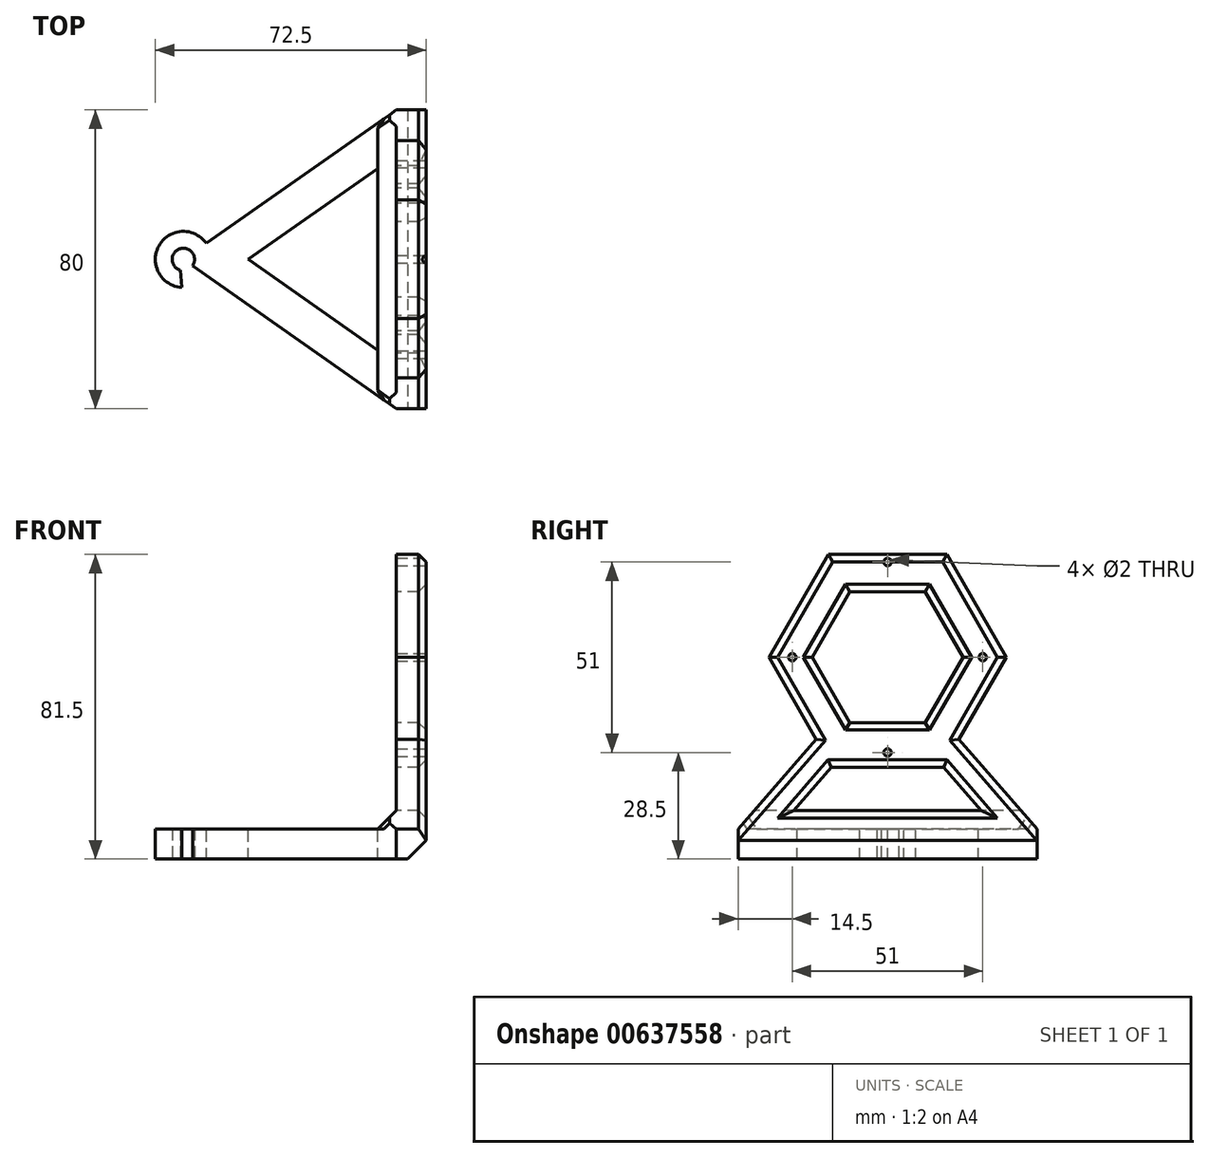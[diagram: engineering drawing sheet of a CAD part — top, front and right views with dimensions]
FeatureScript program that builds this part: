
annotation { "Feature Type Name" : "Feature", "Feature Type Description" : "" }
export const myFeature = defineFeature(function(context is Context, id is Id, definition is map)
    precondition{}
    {
        {
            var Q0;
            Q0=qCreatedBy(makeId("Front.planeOp"),FACE);
            var sketch = newSketch(context, id + "F0", { "sketchPlane" : qUnion([Q0])});
            skLineSegment(sketch, "E0", {"start": v(0, 0) * mm, "end": v(-90, 0) * mm});
            skLineSegment(sketch, "E1", {"start": v(0, 0) * mm, "end": v(0, 100) * mm});
            skLineSegment(sketch, "E2", {"start": v(0, 100) * mm, "end": v(-8, 100) * mm});
            skLineSegment(sketch, "E3", {"start": v(-8, 100) * mm, "end": v(-8, 8) * mm});
            skLineSegment(sketch, "E4", {"start": v(-8, 8) * mm, "end": v(-90, 8) * mm});
            skLineSegment(sketch, "E5", {"start": v(-90, 8) * mm, "end": v(-90, 0) * mm});
            skSolve(sketch);
        }
        {
            var Q0;
            Q0 = qSketchRegion(id + "F0", true);
            extrude(context, id + "F1", {"entities" : qUnion([Q0]), "endBound" : BoundingType.SYMMETRIC, "depth" : 80 * mm, "offsetDistance" : 25 * mm});
        }
        {
            var Q0;
            Q0=makeQuery(id+"F1.opExtrude","SWEPT_FACE",FACE,{"disambiguationData":[OSD([sQuery(id+"F0.wireOp",EDGE,"E0")])]});
            var sketch = newSketch(context, id + "F2", { "sketchPlane" : qUnion([Q0])});
            skCircle(sketch, "E6", {"center": v(-65, 0) * mm, "radius": 3 * mm});
            skSolve(sketch);
        }
        {
            var Q0;
            Q0 = qSketchRegion(id + "F2", true);
            extrude(context, id + "F3", {"entities" : qUnion([Q0]), "operationType" : NewBodyOperationType.REMOVE, "endBound" : BoundingType.THROUGH_ALL, "oppositeDirection" : true, "depth" : 25 * mm, "offsetDistance" : 25 * mm});
        }
        {
            var Q0;
            Q0=makeQuery(id+"F1.opExtrude","SWEPT_FACE",FACE,{"disambiguationData":[OSD([sQuery(id+"F0.wireOp",EDGE,"E1")])]});
            var sketch = newSketch(context, id + "F4", { "sketchPlane" : qUnion([Q0])});
            skLineSegment(sketch, "E7", {"start": v(-40, 100) * mm, "end": v(40, 8) * mm, "construction": true});
            skLineSegment(sketch, "E8", {"start": v(40, 100) * mm, "end": v(-40, 8) * mm, "construction": true});
            skPoint(sketch, "E9", {"position": v(-25.5, 54) * mm});
            skLineSegment(sketch, "E10", {"start": v(0, 54) * mm, "end": v(0, 99.75) * mm, "construction": true});
            skLineSegment(sketch, "E11", {"start": v(0, 54) * mm, "end": v(-45.17, 54) * mm, "construction": true});
            skPoint(sketch, "E12.1.0", {"position": v(0, 28.5) * mm});
            skPoint(sketch, "E12.2.0", {"position": v(25.5, 54) * mm});
            skPoint(sketch, "E12.3.0", {"position": v(0, 79.5) * mm});
            skPoint(sketch, "E12.center", {"position": v(0, 54) * mm});
            skSolve(sketch);
        }
        {
            var Q0;
            Q0=sQuery(id+"F4.wireOp",VERTEX,"E9");
            var Q1;
            Q1=sQuery(id+"F4.wireOp",VERTEX,"E12.3.0");
            var Q2;
            Q2=sQuery(id+"F4.wireOp",VERTEX,"E12.2.0");
            var Q3;
            Q3=sQuery(id+"F4.wireOp",VERTEX,"E12.1.0");
            var Q4;
            Q4=makeQuery(id+"F1.opExtrude","SWEPT_BODY",BODY,{"disambiguationData":[OSD([sQuery(id+"F0.wireOp",EDGE,"E0"),sQuery(id+"F0.wireOp",EDGE,"E1"),sQuery(id+"F0.wireOp",EDGE,"E2"),sQuery(id+"F0.wireOp",EDGE,"E3"),sQuery(id+"F0.wireOp",EDGE,"E4"),sQuery(id+"F0.wireOp",EDGE,"E5")])]});
            hole(context, id + "F5", {"style" : HoleStyle.C_BORE, "endStyle" : HoleEndStyle.THROUGH, "holeDiameter" : 2 * mm, "cBoreDiameter" : 6.5 * mm, "cBoreDepth" : 0 * mm, "majorDiameter" : 3 * mm, "isTappedThrough" : true, "tappedDepth" : 12 * mm, "tapClearance" : 3, "locations" : qUnion([Q0, Q1, Q2, Q3]), "scope" : qUnion([Q4])});
        }
        {
            var Q0;
            Q0=makeQuery(id+"F1.opExtrude","SWEPT_FACE",FACE,{"disambiguationData":[OSD([sQuery(id+"F0.wireOp",EDGE,"E3")])]});
            var sketch = newSketch(context, id + "F6", { "sketchPlane" : qUnion([Q0])});
            skLineSegment(sketch, "E13", {"start": v(-40, 100) * mm, "end": v(40, 8) * mm, "construction": true});
            skLineSegment(sketch, "E14", {"start": v(40, 100) * mm, "end": v(-40, 8) * mm, "construction": true});
            skCircle(sketch, "E15.cCircle", {"center": v(0, 54) * mm, "radius": 27.5 * mm, "construction": true});
            skLineSegment(sketch, "E15.1", {"start": v(-19.08, 32.05) * mm, "end": v(-31.75, 54) * mm});
            skLineSegment(sketch, "E15.2", {"start": v(-31.75, 54) * mm, "end": v(-15.88, 81.5) * mm});
            skLineSegment(sketch, "E15.3", {"start": v(-15.88, 81.5) * mm, "end": v(15.88, 81.5) * mm});
            skLineSegment(sketch, "E15.4", {"start": v(15.88, 81.5) * mm, "end": v(31.75, 54) * mm});
            skLineSegment(sketch, "E15.5", {"start": v(31.75, 54) * mm, "end": v(19.08, 32.05) * mm});
            skPoint(sketch, "E15.0.midPoint", {"position": v(0, 26.5) * mm});
            skLineSegment(sketch, "E16", {"start": v(-40, 8) * mm, "end": v(-19.08, 32.05) * mm});
            skLineSegment(sketch, "E17", {"start": v(40, 8) * mm, "end": v(19.08, 32.05) * mm});
            skPoint(sketch, "E18.orphan", {"position": v(-15.88, 26.5) * mm});
            skPoint(sketch, "E19.orphan", {"position": v(15.88, 26.5) * mm});
            skCircle(sketch, "E20.cCircle", {"center": v(0, 54) * mm, "radius": 17.5 * mm, "construction": true});
            skLineSegment(sketch, "E20.0", {"start": v(10.1, 36.5) * mm, "end": v(-10.1, 36.5) * mm});
            skLineSegment(sketch, "E20.1", {"start": v(-10.1, 36.5) * mm, "end": v(-20.2, 54) * mm});
            skLineSegment(sketch, "E20.2", {"start": v(-20.2, 54) * mm, "end": v(-10.1, 71.5) * mm});
            skLineSegment(sketch, "E20.3", {"start": v(-10.1, 71.5) * mm, "end": v(10.1, 71.5) * mm});
            skLineSegment(sketch, "E20.4", {"start": v(10.1, 71.5) * mm, "end": v(20.2, 54) * mm});
            skLineSegment(sketch, "E20.5", {"start": v(20.2, 54) * mm, "end": v(10.1, 36.5) * mm});
            skPoint(sketch, "E20.0.midPoint", {"position": v(0, 36.5) * mm});
            skLineSegment(sketch, "E21.0", {"start": v(-40, 100) * mm, "end": v(-40, 8) * mm});
            skLineSegment(sketch, "E22.0", {"start": v(40, 100) * mm, "end": v(-40, 100) * mm});
            skLineSegment(sketch, "E23.0", {"start": v(40, 100) * mm, "end": v(40, 8) * mm});
            skLineSegment(sketch, "E24", {"start": v(-25.05, 13) * mm, "end": v(-15.05, 24.5) * mm});
            skLineSegment(sketch, "E25", {"start": v(-15.05, 24.5) * mm, "end": v(15.05, 24.5) * mm});
            skLineSegment(sketch, "E26", {"start": v(15.05, 24.5) * mm, "end": v(25.05, 13) * mm});
            skLineSegment(sketch, "E27", {"start": v(25.05, 13) * mm, "end": v(-25.05, 13) * mm});
            skSolve(sketch);
        }
        {
            var Q0;
            Q0=makeQuery(id+"F6.imprint","IMPRINT",FACE,{"disambiguationData":[TD([[makeQuery(id+"F6.imprint","IMPRINT",EDGE,{"derivedFrom":sQuery(id+"F6.wireOp",EDGE,"E15.1")}),1.0]])]});
            var Q1;
            Q1=makeQuery(id+"F6.imprint","IMPRINT",FACE,{"disambiguationData":[TD([[makeQuery(id+"F6.imprint","IMPRINT",EDGE,{"derivedFrom":sQuery(id+"F6.wireOp",EDGE,"E20.0")}),-1.0]])]});
            var Q2;
            Q2=makeQuery(id+"F6.imprint","IMPRINT",FACE,{"disambiguationData":[TD([[makeQuery(id+"F6.imprint","IMPRINT",EDGE,{"derivedFrom":sQuery(id+"F6.wireOp",EDGE,"E24")}),-1.0]])]});
            extrude(context, id + "F7", {"entities" : qUnion([Q0, Q1, Q2]), "operationType" : NewBodyOperationType.REMOVE, "endBound" : BoundingType.THROUGH_ALL, "oppositeDirection" : true, "depth" : 25 * mm, "offsetDistance" : 25 * mm});
        }
        {
            var Q0;
            Q0=makeQuery(id+"F1.opExtrude","SWEPT_FACE",FACE,{"disambiguationData":[OSD([sQuery(id+"F0.wireOp",EDGE,"E4")])]});
            var sketch = newSketch(context, id + "F8", { "sketchPlane" : qUnion([Q0])});
            skLineSegment(sketch, "E28.0", {"start": v(-8, 40) * mm, "end": v(-90, 40) * mm});
            skLineSegment(sketch, "E29.0", {"start": v(-90, -40) * mm, "end": v(-90, 40) * mm});
            skLineSegment(sketch, "E30.0", {"start": v(-8, -40) * mm, "end": v(-90, -40) * mm});
            skArc(sketch, "E31", {"start": v(-58.86, 4.3) * mm, "mid": v(-72.5, 0) * mm, "end": v(-58.86, -4.3) * mm});
            skLineSegment(sketch, "E32", {"start": v(-8, 40) * mm, "end": v(-58.86, 4.3) * mm});
            skLineSegment(sketch, "E33", {"start": v(-58.86, -4.3) * mm, "end": v(-8, -40) * mm});
            skLineSegment(sketch, "E34.0", {"start": v(-13, 24.27) * mm, "end": v(-13, -24.27) * mm});
            skLineSegment(sketch, "E34.1", {"start": v(-13, -24.27) * mm, "end": v(-47.6, 0) * mm});
            skLineSegment(sketch, "E34.2", {"start": v(-47.6, 0) * mm, "end": v(-13, 24.27) * mm});
            skPoint(sketch, "E34.0.midPoint", {"position": v(-13, 0) * mm});
            skLineSegment(sketch, "E35", {"start": v(-65, 0) * mm, "end": v(8.93, 0) * mm, "construction": true});
            skSolve(sketch);
        }
        {
            var Q0;
            Q0=makeQuery(id+"F8.imprint","IMPRINT",FACE,{"disambiguationData":[TD([[makeQuery(id+"F8.imprint","IMPRINT",EDGE,{"derivedFrom":sQuery(id+"F8.wireOp",EDGE,"E28.0")}),1.0]])]});
            var Q1;
            Q1=makeQuery(id+"F8.imprint","IMPRINT",FACE,{"disambiguationData":[TD([[makeQuery(id+"F8.imprint","IMPRINT",EDGE,{"derivedFrom":sQuery(id+"F8.wireOp",EDGE,"E34.0")}),-1.0]])]});
            extrude(context, id + "F9", {"entities" : qUnion([Q0, Q1]), "operationType" : NewBodyOperationType.REMOVE, "endBound" : BoundingType.THROUGH_ALL, "oppositeDirection" : true, "depth" : 25 * mm, "offsetDistance" : 25 * mm});
        }
        {
            var Q0;
            Q0=makeQuery(id+"F1.opExtrude","SWEPT_EDGE",EDGE,{"disambiguationData":[OSD([sQuery(id+"F0.wireOp",EDGE,"E3"),sQuery(id+"F0.wireOp",EDGE,"E4")])]});
            var Q1;
            Q1=makeQuery(id+"F1.opExtrude","SWEPT_EDGE",EDGE,{"disambiguationData":[OSD([sQuery(id+"F0.wireOp",EDGE,"E0"),sQuery(id+"F0.wireOp",EDGE,"E1")])]});
            chamfer(context, id + "F10", {"entities" : qUnion([Q0, Q1]), "width" : 5 * mm, "tangentPropagation" : true});
        }
        {
            var Q0;
            Q0=makeQuery(id+"F9.boolean.opBoolean","COPY",EDGE,{"derivedFrom":makeQuery(id+"F9.opExtrude","CAP_EDGE",EDGE,{"disambiguationData":[OSD([sQuery(id+"F8.wireOp",EDGE,"E31")])],"isStart":true})});
            var Q1;
            Q1=makeQuery(id+"F9.boolean.opBoolean","COPY",EDGE,{"derivedFrom":makeQuery(id+"F9.opExtrude","CAP_EDGE",EDGE,{"disambiguationData":[OSD([sQuery(id+"F8.wireOp",EDGE,"E33")])],"isStart":true})});
            var Q2;
            Q2=makeQuery(id+"F7.boolean.opBoolean","COPY",EDGE,{"derivedFrom":makeQuery(id+"F7.opExtrude","CAP_EDGE",EDGE,{"disambiguationData":[OSD([sQuery(id+"F6.wireOp",EDGE,"E16")])],"isStart":true})});
            var Q3;
            Q3=makeQuery(id+"F7.boolean.opBoolean","INTERSECT",EDGE,{"derivedFrom":[makeQuery(id+"F1.opExtrude","SWEPT_FACE",FACE,{"disambiguationData":[OSD([sQuery(id+"F0.wireOp",EDGE,"E1")])]}),makeQuery(id+"F7.opExtrude","SWEPT_FACE",FACE,{"disambiguationData":[OSD([sQuery(id+"F6.wireOp",EDGE,"E16")])]})]});
            var Q4;
            Q4=makeQuery(id+"F7.boolean.opBoolean","INTERSECT",EDGE,{"derivedFrom":[makeQuery(id+"F1.opExtrude","SWEPT_FACE",FACE,{"disambiguationData":[OSD([sQuery(id+"F0.wireOp",EDGE,"E1")])]}),makeQuery(id+"F7.opExtrude","SWEPT_FACE",FACE,{"disambiguationData":[OSD([sQuery(id+"F6.wireOp",EDGE,"E15.1")])]})]});
            var Q5;
            Q5=makeQuery(id+"F7.boolean.opBoolean","COPY",EDGE,{"derivedFrom":makeQuery(id+"F7.opExtrude","CAP_EDGE",EDGE,{"disambiguationData":[OSD([sQuery(id+"F6.wireOp",EDGE,"E15.1")])],"isStart":true})});
            var Q6;
            Q6=makeQuery(id+"F7.boolean.opBoolean","COPY",EDGE,{"derivedFrom":makeQuery(id+"F7.opExtrude","CAP_EDGE",EDGE,{"disambiguationData":[OSD([sQuery(id+"F6.wireOp",EDGE,"E15.2")])],"isStart":true})});
            var Q7;
            Q7=makeQuery(id+"F7.boolean.opBoolean","INTERSECT",EDGE,{"derivedFrom":[makeQuery(id+"F1.opExtrude","SWEPT_FACE",FACE,{"disambiguationData":[OSD([sQuery(id+"F0.wireOp",EDGE,"E1")])]}),makeQuery(id+"F7.opExtrude","SWEPT_FACE",FACE,{"disambiguationData":[OSD([sQuery(id+"F6.wireOp",EDGE,"E15.2")])]})]});
            var Q8;
            Q8=makeQuery(id+"F7.boolean.opBoolean","COPY",EDGE,{"derivedFrom":makeQuery(id+"F7.opExtrude","CAP_EDGE",EDGE,{"disambiguationData":[OSD([sQuery(id+"F6.wireOp",EDGE,"E15.3")])],"isStart":true})});
            var Q9;
            Q9=makeQuery(id+"F7.boolean.opBoolean","INTERSECT",EDGE,{"derivedFrom":[makeQuery(id+"F1.opExtrude","SWEPT_FACE",FACE,{"disambiguationData":[OSD([sQuery(id+"F0.wireOp",EDGE,"E1")])]}),makeQuery(id+"F7.opExtrude","SWEPT_FACE",FACE,{"disambiguationData":[OSD([sQuery(id+"F6.wireOp",EDGE,"E15.3")])]})]});
            var Q10;
            Q10=makeQuery(id+"F7.boolean.opBoolean","INTERSECT",EDGE,{"derivedFrom":[makeQuery(id+"F1.opExtrude","SWEPT_FACE",FACE,{"disambiguationData":[OSD([sQuery(id+"F0.wireOp",EDGE,"E1")])]}),makeQuery(id+"F7.opExtrude","SWEPT_FACE",FACE,{"disambiguationData":[OSD([sQuery(id+"F6.wireOp",EDGE,"E15.4")])]})]});
            var Q11;
            Q11=makeQuery(id+"F7.boolean.opBoolean","COPY",EDGE,{"derivedFrom":makeQuery(id+"F7.opExtrude","CAP_EDGE",EDGE,{"disambiguationData":[OSD([sQuery(id+"F6.wireOp",EDGE,"E15.4")])],"isStart":true})});
            var Q12;
            Q12=makeQuery(id+"F7.boolean.opBoolean","COPY",EDGE,{"derivedFrom":makeQuery(id+"F7.opExtrude","CAP_EDGE",EDGE,{"disambiguationData":[OSD([sQuery(id+"F6.wireOp",EDGE,"E15.5")])],"isStart":true})});
            var Q13;
            Q13=makeQuery(id+"F7.boolean.opBoolean","COPY",EDGE,{"derivedFrom":makeQuery(id+"F7.opExtrude","CAP_EDGE",EDGE,{"disambiguationData":[OSD([sQuery(id+"F6.wireOp",EDGE,"E17")])],"isStart":true})});
            var Q14;
            Q14=makeQuery(id+"F7.boolean.opBoolean","INTERSECT",EDGE,{"derivedFrom":[makeQuery(id+"F1.opExtrude","SWEPT_FACE",FACE,{"disambiguationData":[OSD([sQuery(id+"F0.wireOp",EDGE,"E1")])]}),makeQuery(id+"F7.opExtrude","SWEPT_FACE",FACE,{"disambiguationData":[OSD([sQuery(id+"F6.wireOp",EDGE,"E17")])]})]});
            var Q15;
            Q15=makeQuery(id+"F7.boolean.opBoolean","INTERSECT",EDGE,{"derivedFrom":[makeQuery(id+"F1.opExtrude","SWEPT_FACE",FACE,{"disambiguationData":[OSD([sQuery(id+"F0.wireOp",EDGE,"E1")])]}),makeQuery(id+"F7.opExtrude","SWEPT_FACE",FACE,{"disambiguationData":[OSD([sQuery(id+"F6.wireOp",EDGE,"E15.5")])]})]});
            var Q16;
            Q16=makeQuery(id+"F7.boolean.opBoolean","COPY",EDGE,{"derivedFrom":makeQuery(id+"F7.opExtrude","CAP_EDGE",EDGE,{"disambiguationData":[OSD([sQuery(id+"F6.wireOp",EDGE,"E20.0")])],"isStart":true})});
            var Q17;
            Q17=makeQuery(id+"F7.boolean.opBoolean","COPY",EDGE,{"derivedFrom":makeQuery(id+"F7.opExtrude","CAP_EDGE",EDGE,{"disambiguationData":[OSD([sQuery(id+"F6.wireOp",EDGE,"E20.5")])],"isStart":true})});
            var Q18;
            Q18=makeQuery(id+"F7.boolean.opBoolean","COPY",EDGE,{"derivedFrom":makeQuery(id+"F7.opExtrude","CAP_EDGE",EDGE,{"disambiguationData":[OSD([sQuery(id+"F6.wireOp",EDGE,"E20.4")])],"isStart":true})});
            var Q19;
            Q19=makeQuery(id+"F7.boolean.opBoolean","COPY",EDGE,{"derivedFrom":makeQuery(id+"F7.opExtrude","CAP_EDGE",EDGE,{"disambiguationData":[OSD([sQuery(id+"F6.wireOp",EDGE,"E20.3")])],"isStart":true})});
            var Q20;
            Q20=makeQuery(id+"F7.boolean.opBoolean","COPY",EDGE,{"derivedFrom":makeQuery(id+"F7.opExtrude","CAP_EDGE",EDGE,{"disambiguationData":[OSD([sQuery(id+"F6.wireOp",EDGE,"E20.2")])],"isStart":true})});
            var Q21;
            Q21=makeQuery(id+"F7.boolean.opBoolean","COPY",EDGE,{"derivedFrom":makeQuery(id+"F7.opExtrude","CAP_EDGE",EDGE,{"disambiguationData":[OSD([sQuery(id+"F6.wireOp",EDGE,"E20.1")])],"isStart":true})});
            var Q22;
            Q22=makeQuery(id+"F7.boolean.opBoolean","INTERSECT",EDGE,{"derivedFrom":[makeQuery(id+"F1.opExtrude","SWEPT_FACE",FACE,{"disambiguationData":[OSD([sQuery(id+"F0.wireOp",EDGE,"E1")])]}),makeQuery(id+"F7.opExtrude","SWEPT_FACE",FACE,{"disambiguationData":[OSD([sQuery(id+"F6.wireOp",EDGE,"E20.1")])]})]});
            var Q23;
            Q23=makeQuery(id+"F7.boolean.opBoolean","INTERSECT",EDGE,{"derivedFrom":[makeQuery(id+"F1.opExtrude","SWEPT_FACE",FACE,{"disambiguationData":[OSD([sQuery(id+"F0.wireOp",EDGE,"E1")])]}),makeQuery(id+"F7.opExtrude","SWEPT_FACE",FACE,{"disambiguationData":[OSD([sQuery(id+"F6.wireOp",EDGE,"E20.0")])]})]});
            var Q24;
            Q24=makeQuery(id+"F7.boolean.opBoolean","INTERSECT",EDGE,{"derivedFrom":[makeQuery(id+"F1.opExtrude","SWEPT_FACE",FACE,{"disambiguationData":[OSD([sQuery(id+"F0.wireOp",EDGE,"E1")])]}),makeQuery(id+"F7.opExtrude","SWEPT_FACE",FACE,{"disambiguationData":[OSD([sQuery(id+"F6.wireOp",EDGE,"E20.5")])]})]});
            var Q25;
            Q25=makeQuery(id+"F7.boolean.opBoolean","INTERSECT",EDGE,{"derivedFrom":[makeQuery(id+"F1.opExtrude","SWEPT_FACE",FACE,{"disambiguationData":[OSD([sQuery(id+"F0.wireOp",EDGE,"E1")])]}),makeQuery(id+"F7.opExtrude","SWEPT_FACE",FACE,{"disambiguationData":[OSD([sQuery(id+"F6.wireOp",EDGE,"E20.4")])]})]});
            var Q26;
            Q26=makeQuery(id+"F7.boolean.opBoolean","INTERSECT",EDGE,{"derivedFrom":[makeQuery(id+"F1.opExtrude","SWEPT_FACE",FACE,{"disambiguationData":[OSD([sQuery(id+"F0.wireOp",EDGE,"E1")])]}),makeQuery(id+"F7.opExtrude","SWEPT_FACE",FACE,{"disambiguationData":[OSD([sQuery(id+"F6.wireOp",EDGE,"E20.3")])]})]});
            var Q27;
            Q27=makeQuery(id+"F7.boolean.opBoolean","INTERSECT",EDGE,{"derivedFrom":[makeQuery(id+"F1.opExtrude","SWEPT_FACE",FACE,{"disambiguationData":[OSD([sQuery(id+"F0.wireOp",EDGE,"E1")])]}),makeQuery(id+"F7.opExtrude","SWEPT_FACE",FACE,{"disambiguationData":[OSD([sQuery(id+"F6.wireOp",EDGE,"E20.2")])]})]});
            var Q28;
            Q28=makeQuery(id+"F9.boolean.opBoolean","COPY",EDGE,{"derivedFrom":makeQuery(id+"F9.opExtrude","CAP_EDGE",EDGE,{"disambiguationData":[OSD([sQuery(id+"F8.wireOp",EDGE,"E32")])],"isStart":true})});
            var Q29;
            Q29=makeQuery(id+"F10.opChamfer","BLEND_EDGE",EDGE,{"blendedFrom":[makeQuery(id+"F1.opExtrude","SWEPT_EDGE",EDGE,{"disambiguationData":[OSD([sQuery(id+"F0.wireOp",EDGE,"E3"),sQuery(id+"F0.wireOp",EDGE,"E4")])]}),makeQuery(id+"F9.boolean.opBoolean","COPY",FACE,{"derivedFrom":makeQuery(id+"F9.opExtrude","SWEPT_FACE",FACE,{"disambiguationData":[OSD([sQuery(id+"F8.wireOp",EDGE,"E32")])]})})],"blendedInto":[makeQuery(id+"F9.boolean.opBoolean","COPY",FACE,{"derivedFrom":makeQuery(id+"F9.opExtrude","SWEPT_FACE",FACE,{"disambiguationData":[OSD([sQuery(id+"F8.wireOp",EDGE,"E32")])]})})]});
            var Q30;
            Q30=makeQuery(id+"F10.opChamfer","BLEND_EDGE",EDGE,{"blendedFrom":[makeQuery(id+"F1.opExtrude","SWEPT_EDGE",EDGE,{"disambiguationData":[OSD([sQuery(id+"F0.wireOp",EDGE,"E3"),sQuery(id+"F0.wireOp",EDGE,"E4")])]}),makeQuery(id+"F9.boolean.opBoolean","COPY",FACE,{"derivedFrom":makeQuery(id+"F9.opExtrude","SWEPT_FACE",FACE,{"disambiguationData":[OSD([sQuery(id+"F8.wireOp",EDGE,"E33")])]})})],"blendedInto":[makeQuery(id+"F9.boolean.opBoolean","COPY",FACE,{"derivedFrom":makeQuery(id+"F9.opExtrude","SWEPT_FACE",FACE,{"disambiguationData":[OSD([sQuery(id+"F8.wireOp",EDGE,"E33")])]})})]});
            var Q31;
            Q31=makeQuery(id+"F7.boolean.opBoolean","INTERSECT",EDGE,{"derivedFrom":[makeQuery(id+"F1.opExtrude","SWEPT_FACE",FACE,{"disambiguationData":[OSD([sQuery(id+"F0.wireOp",EDGE,"E1")])]}),makeQuery(id+"F7.opExtrude","SWEPT_FACE",FACE,{"disambiguationData":[OSD([sQuery(id+"F6.wireOp",EDGE,"E27")])]})]});
            var Q32;
            Q32=makeQuery(id+"F7.boolean.opBoolean","INTERSECT",EDGE,{"derivedFrom":[makeQuery(id+"F1.opExtrude","SWEPT_FACE",FACE,{"disambiguationData":[OSD([sQuery(id+"F0.wireOp",EDGE,"E1")])]}),makeQuery(id+"F7.opExtrude","SWEPT_FACE",FACE,{"disambiguationData":[OSD([sQuery(id+"F6.wireOp",EDGE,"E26")])]})]});
            var Q33;
            Q33=makeQuery(id+"F7.boolean.opBoolean","INTERSECT",EDGE,{"derivedFrom":[makeQuery(id+"F1.opExtrude","SWEPT_FACE",FACE,{"disambiguationData":[OSD([sQuery(id+"F0.wireOp",EDGE,"E1")])]}),makeQuery(id+"F7.opExtrude","SWEPT_FACE",FACE,{"disambiguationData":[OSD([sQuery(id+"F6.wireOp",EDGE,"E25")])]})]});
            var Q34;
            Q34=makeQuery(id+"F7.boolean.opBoolean","INTERSECT",EDGE,{"derivedFrom":[makeQuery(id+"F1.opExtrude","SWEPT_FACE",FACE,{"disambiguationData":[OSD([sQuery(id+"F0.wireOp",EDGE,"E1")])]}),makeQuery(id+"F7.opExtrude","SWEPT_FACE",FACE,{"disambiguationData":[OSD([sQuery(id+"F6.wireOp",EDGE,"E24")])]})]});
            var Q35;
            Q35=makeQuery(id+"F7.boolean.opBoolean","COPY",EDGE,{"derivedFrom":makeQuery(id+"F7.opExtrude","CAP_EDGE",EDGE,{"disambiguationData":[OSD([sQuery(id+"F6.wireOp",EDGE,"E24")])],"isStart":true})});
            var Q36;
            Q36=makeQuery(id+"F7.boolean.opBoolean","COPY",EDGE,{"derivedFrom":makeQuery(id+"F7.opExtrude","CAP_EDGE",EDGE,{"disambiguationData":[OSD([sQuery(id+"F6.wireOp",EDGE,"E25")])],"isStart":true})});
            var Q37;
            Q37=makeQuery(id+"F7.boolean.opBoolean","COPY",EDGE,{"derivedFrom":makeQuery(id+"F7.opExtrude","CAP_EDGE",EDGE,{"disambiguationData":[OSD([sQuery(id+"F6.wireOp",EDGE,"E26")])],"isStart":true})});
            chamfer(context, id + "F11", {"entities" : qUnion([Q0, Q1, Q2, Q3, Q4, Q5, Q6, Q7, Q8, Q9, Q10, Q11, Q12, Q13, Q14, Q15, Q16, Q17, Q18, Q19, Q20, Q21, Q22, Q23, Q24, Q25, Q26, Q27, Q28, Q29, Q30, Q31, Q32, Q33, Q34, Q35, Q36, Q37]), "width" : 2 * mm, "tangentPropagation" : true});
        }
        {
            var Q0;
            Q0=makeQuery(id+"F1.opExtrude","SWEPT_FACE",FACE,{"disambiguationData":[OSD([sQuery(id+"F0.wireOp",EDGE,"E4")])]});
            var sketch = newSketch(context, id + "F12", { "sketchPlane" : qUnion([Q0])});
            skLineSegment(sketch, "E36", {"start": v(-56.3, -6.1) * mm, "end": v(-65, 0) * mm});
            skLineSegment(sketch, "E37", {"start": v(-65, 0) * mm, "end": v(-65.92, -1.3) * mm});
            skLineSegment(sketch, "E38", {"start": v(-65.92, -1.3) * mm, "end": v(-65, -11.98) * mm});
            skLineSegment(sketch, "E39", {"start": v(-65, -11.98) * mm, "end": v(-56.3, -6.1) * mm});
            skSolve(sketch);
        }
        {
            var Q0;
            {var subQ0=sQuery(id+"F12.wireOp",EDGE,"E39");Q0=makeQuery(id+"F12.imprint","IMPRINT",FACE,{"disambiguationData":[TD([[makeQuery(id+"F12.imprint","IMPRINT",EDGE,{"derivedFrom":subQ0}),1.0]])]});}
            var Q1;
            {var subQ0=sQuery(id+"F12.wireOp",EDGE,"E36");var subQ1=makeQuery(id+"F1.opExtrude","SWEPT_FACE",FACE,{"disambiguationData":[OSD([sQuery(id+"F0.wireOp",EDGE,"E4")])]});var subQ2=makeQuery(id+"F11.opChamfer","BLEND_EDGE",EDGE,{"blendedFrom":[makeQuery(id+"F9.boolean.opBoolean","COPY",EDGE,{"derivedFrom":makeQuery(id+"F9.opExtrude","CAP_EDGE",EDGE,{"disambiguationData":[OSD([sQuery(id+"F8.wireOp",EDGE,"E31")])],"isStart":true})}),subQ1],"blendedInto":[subQ1]});var subQ3=makeQuery(id+"F12.imprint","INTERSECT",VERTEX,{"derivedFrom":[subQ2,subQ0]});Q1=makeQuery(id+"F12.imprint","IMPRINT",FACE,{"disambiguationData":[TD([[makeQuery(id+"F12.imprint","IMPRINT",EDGE,{"disambiguationData":[TD([[subQ3,-1.0]])],"derivedFrom":subQ0}),1.0]])]});}
            var Q2;
            {var subQ0=sQuery(id+"F12.wireOp",EDGE,"E37");Q2=makeQuery(id+"F12.imprint","IMPRINT",FACE,{"disambiguationData":[TD([[makeQuery(id+"F12.imprint","IMPRINT",EDGE,{"derivedFrom":subQ0}),1.0]])]});}
            extrude(context, id + "F13", {"entities" : qUnion([Q0, Q1, Q2]), "operationType" : NewBodyOperationType.REMOVE, "oppositeDirection" : true, "depth" : 25 * mm, "offsetDistance" : 25 * mm});
        }
    });
